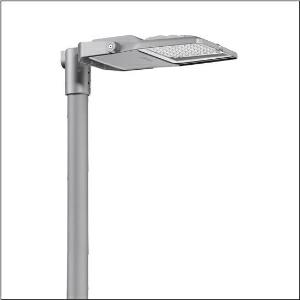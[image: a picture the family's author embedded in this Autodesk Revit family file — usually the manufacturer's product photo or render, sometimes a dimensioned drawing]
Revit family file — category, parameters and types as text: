
# Revit family: floodlight_fl_21_iq_mini___pl61_5xa7772c4c3a_2e37
name_source: partatom
category: Lighting Fixtures
units: mm (PartAtom-declared; Revit-internal decimal feet)

## family parameters
Cut with Voids When Loaded = No
Host = Face
Light Source = No
Part Type = Normal
Room Calculation Point = No
Round Connector Dimension = Use Diameter
Shared = No

## types (1)
- --- (1 x LED, 12490 lm, 87.2 W, 4000K)
    Apparent Load = 87 VA
    CIE Flux Codes = 33 65 98 100 100
    Color Rendering = 70
    Color Temperature = 4000K
    Default Elevation = 1800 mm
    Description = Floodlight FL 21 iQ mini, floodlight, primary light control with lens, of PMMA, primary optical cover: protective disc, of toughened safety glass, transparent, light distribution: PL61, light emission: direct distribution, installation type: surface-mounted, LED, High Power LED, rated luminous flux: 12.490lm, luminous efficacy: 143lm/W, light colour: 740, colour temperature: 4000K, control: Auto-Match, Temp-Guard, Night-Set, Smart-Wire, Desk-Remote (wireless, voltage-free reading and setting of iQ features in the workshop via application-optimized NFC function/RFID function), optimised constant luminous flux control (CLO 2.0), Light-Fading, Lumen-Switch, with terminal, 6-pole, mains connection: 220..240V, AC, 50/60Hz, start of lifetime: 87W, end of service life: 92W, reduction: 40W, luminaire housing, of diecast aluminium, powder-coated, Siteco® metallic grey (DB 702S), corrosivity category C5 mid according to DIN EN ISO 12944, sealing non-destructively replaceable, please order mast flange separately, mast bracket, of steel, galvanised, powder-coated, protection rating (complete): IP66, insulation class (complete): insulation class II (safety insulation), certification: CE, ENEC, VDE, protection symbol: D, impact resistance: IK08, permissible operating ambient temperature: -40..+40°C, permissible operating ambient temperature for outdoor applications: -40..+50°C, standard: DIN EN 12944, LABS conformity tested according to VDMA 24364:2018-05, packaging unit: 1 piece

Light Distribution: PL61
    Height = 70 mm
    Lamp = 1 x LED
    Lamp Light Flux = 12490 lm
    Lamp Power = 87.2 W
    Lamp count = 1
    Length = 485 mm
    Luminous efficacy = 143 lm/W
    Manufacturer = Siteco
    ModVariant = No
    Model = 5XA7772C4C3A
    Number of Poles = 1
    OnlyDefault = Yes
    Power Factor = 1
    Product Name = Floodlight FL 21 iQ mini | PL61
    Product group = floodlight | pylon annexe
    ProductGroupID = 6200
    Protection Class = Protection class II
    Protection Degree = IP 66
    RLX_Detail_Level = 1
    RLX_Emergency_Light_Flux = 0 lm
    RLX_Emergency_Type = 0
    RLX_Emergency_Type_DB = No
    RlxData = <blob elided: 101353 chars, md5=0cec0016>
    Socket = socket
    Standby Power = 0 W
    System Light Flux = 12490 lm
    System Power = 87 W
    Type Comments = factory setting: luminous flux: 100 % | dim-lin: 254 | 456 mA
    Type Image = l_1007125.jpg
    URL = http://relux.com
    VarID = @adj_123827
    Voltage = 0 V
    Weight = 0.00 kg
    Width = 337 mm

## geometry (parser evidence)
native form markers: Blend x4, Sweep x10
no freeform markers — native parametric forms only
